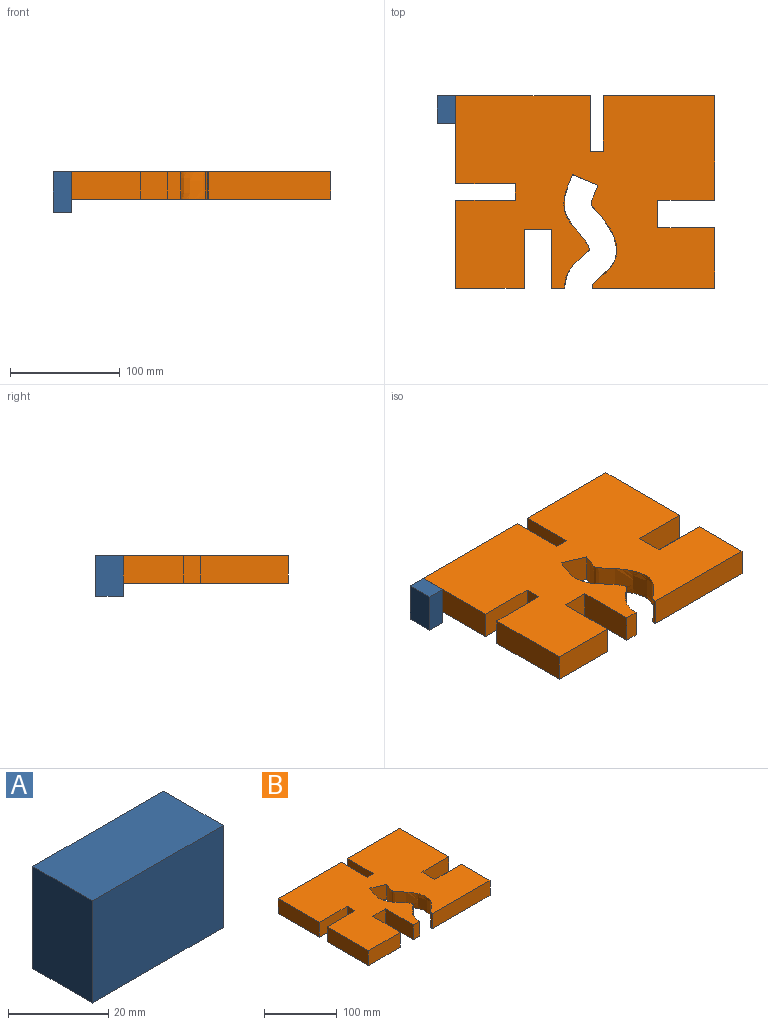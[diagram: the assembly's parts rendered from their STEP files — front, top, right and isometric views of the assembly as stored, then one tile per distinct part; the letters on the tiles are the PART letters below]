
ASSEMBLY  parts=2 mates=1
PART A: 6 faces, bbox 37x16.9x25 mm
  f0: plane 36.98x25mm, normal (0,-1,0), area 924.5mm2, adj f1,f3,f4,f5
  f1: plane 25x16.87mm, normal (1,0,0), area 421.7mm2, adj f0,f2,f4,f5
  f2: plane 36.98x25mm, normal (0,1,0), area 924.5mm2, adj f1,f3,f4,f5
  f3: plane 25x16.87mm, normal (-1,0,0), area 421.7mm2, adj f0,f2,f4,f5
  f4: plane 36.98x16.87mm, normal (0,0,1), area 623.7mm2, adj f0,f1,f2,f3
  f5: plane 36.98x16.87mm, normal (0,0,-1), area 623.7mm2, adj f0,f1,f2,f3
PART B: 27 faces, bbox 235.5x175.2x25 mm
  f0: plane 122.11x25mm, normal (0,1,0), area 3052.8mm2, adj f2,f9,f10,f25
  f1: plane 25x12.18mm, normal (0,-1,0), area 304.6mm2, adj f9,f10,f12,f23
  f2: plane 80.1x25mm, normal (-1,0,0), area 2002.5mm2, adj f0,f9,f10,f19
  f3: plane 95.02x25mm, normal (1,0,0), area 2375.5mm2, adj f7,f9,f10,f15
  f4: plane 61.99x25mm, normal (0,-1,0), area 1549.8mm2, adj f8,f9,f10,f13
  f5: plane 111.27x25mm, normal (0,-1,0), area 2781.9mm2, adj f6,f9,f10,f22
  f6: plane 55.18x25mm, normal (1,0,0), area 1379.5mm2, adj f5,f9,f10,f16
  f7: plane 101.41x25mm, normal (0,1,0), area 2535.3mm2, adj f3,f9,f10,f26
  f8: plane 80.1x25mm, normal (-1,0,0), area 2002.5mm2, adj f4,f9,f10,f18
  f9: plane 235.53x175.2mm, normal (0,0,1), area 34337.2mm2, adj f0,f1,f2,f3,f4,f5,f6,f7
  f10: plane 235.53x175.2mm, normal (0,0,-1), area 34337.2mm2, adj f0,f1,f2,f3,f4,f5,f6,f7
  f11: plane 25x25mm, normal (0,-1,0), area 625mm2, adj f9,f10,f12,f13
  f12: plane 53.78x25mm, normal (-1,0,0), area 1344.5mm2, adj f1,f9,f10,f11
  f13: plane 53.78x25mm, normal (1,0,0), area 1344.5mm2, adj f4,f9,f10,f11
  f14: plane 25x25mm, normal (1,0,0), area 625mm2, adj f9,f10,f15,f16
  f15: plane 51.66x25mm, normal (0,-1,0), area 1291.6mm2, adj f3,f9,f10,f14
  f16: plane 51.66x25mm, normal (0,1,0), area 1291.6mm2, adj f6,f9,f10,f14
  f17: plane 25x15mm, normal (-1,0,0), area 375mm2, adj f9,f10,f18,f19
  f18: plane 53.88x25mm, normal (0,1,0), area 1346.9mm2, adj f8,f9,f10,f17
  f19: plane 53.88x25mm, normal (0,-1,0), area 1346.9mm2, adj f2,f9,f10,f17
  f20: plane 25x23.03mm, normal (-0.39,-0.92,0), area 625mm2, adj f9,f10,f21,f22
  f21: extruded ~68.55x25mm, area 1927.8mm2, adj f9,f10,f20,f23
  f22: extruded ~93.75x25mm, area 2739.1mm2, adj f5,f9,f10,f20
  f23: extruded ~34.93x25mm, area 1084mm2, adj f1,f9,f10,f21
  f24: plane 25x12mm, normal (0,1,0), area 300mm2, adj f9,f10,f25,f26
  f25: plane 50.33x25mm, normal (1,0,0), area 1258.2mm2, adj f0,f9,f10,f24
  f26: plane 50.33x25mm, normal (-1,0,0), area 1258.2mm2, adj f7,f9,f10,f24
PLACE A rot(axis=(0.58,-0.58,0.58),120deg) t=(-81.52,112.6,64.7)mm
PLACE B t=(-16.04,0,-52.57)mm
MATE revolute A.f0 <-> B.f2  axis (-1,0,0) through (-133.81,87.6,-27.57)mm
